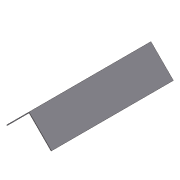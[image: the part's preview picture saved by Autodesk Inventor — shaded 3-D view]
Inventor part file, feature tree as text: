
AUTODESK INVENTOR PART (.ipt)
format: ipt  version: 2012 (Build 160160000, 160)  size: 69,120 bytes
history: native  units: in
note: dims shown in document units (in); Inventor stores cm internally (conversion verified against a paired STEP export)
features: extrude x1, sketch x1
ambient origin geometry x8: Origin, YZ Plane, XZ Plane, XY Plane, X Axis, Y Axis, Z Axis, Center Point
bodies: Solid1 (feature_tree)
feature tree (2):
  extrude  "Extrusion1"  Depth=5.0in
  sketch  "Sketch1"  dims[d0=0.125in d1=5.0in d2=23.0in d3=0.0in]
